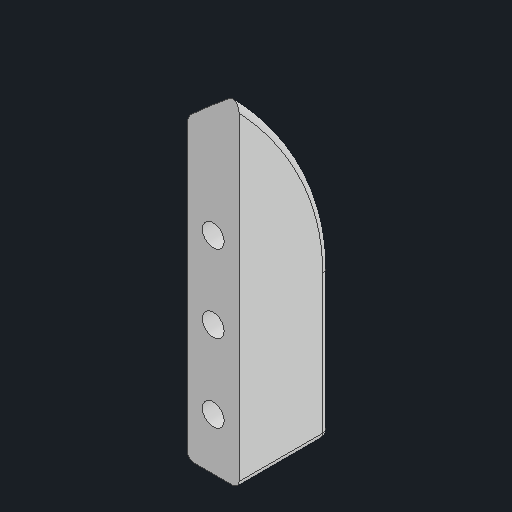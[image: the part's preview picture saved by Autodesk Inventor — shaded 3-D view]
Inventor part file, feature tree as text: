
AUTODESK INVENTOR PART (.ipt)
format: ipt  version: 2024.3 (Build 283343010, 343A)  size: 142,336 bytes
history: native  units: in
note: dims shown in document units (in); Inventor stores cm internally (conversion verified against a paired STEP export)
features: other x3, sketch x2
ambient origin geometry x8: Origin, YZ Plane, XZ Plane, XY Plane, X Axis, Y Axis, Z Axis, Center Point
bodies: Solid1 (feature_tree)
feature tree (5):
  other  "coral_end_stop.ipt"
  other  "Solid1::coral_end_stop.ipt"
  other  "TaggingFeature1"
  sketch  "Sketch1"  dims[d0=0.3937in]
  sketch  "Sketch2"
